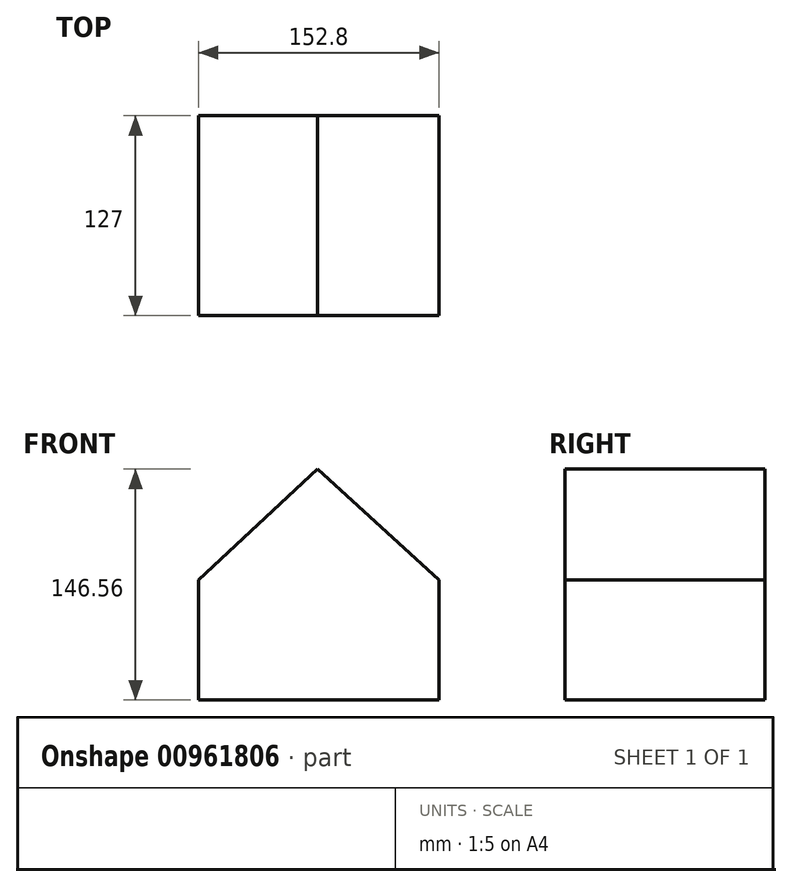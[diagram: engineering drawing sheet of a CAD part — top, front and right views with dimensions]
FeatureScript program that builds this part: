
annotation { "Feature Type Name" : "Feature", "Feature Type Description" : "" }
export const myFeature = defineFeature(function(context is Context, id is Id, definition is map)
    precondition{}
    {
        {
            var Q0;
            Q0=qCreatedBy(makeId("Front.planeOp"),FACE);
            var sketch = newSketch(context, id + "F0", { "sketchPlane" : qUnion([Q0])});
            skLineSegment(sketch, "E0", {"start": v(-75.58, 0) * mm, "end": v(0, 70.33) * mm});
            skLineSegment(sketch, "E1", {"start": v(0, 70.33) * mm, "end": v(77.22, 0) * mm});
            skLineSegment(sketch, "E2", {"start": v(-75.58, 0) * mm, "end": v(-75.58, -76.23) * mm});
            skLineSegment(sketch, "E3", {"start": v(-75.58, -76.23) * mm, "end": v(77.22, -76.23) * mm});
            skLineSegment(sketch, "E4", {"start": v(77.22, -3.11) * mm, "end": v(77.22, -76.23) * mm});
            skLineSegment(sketch, "E5", {"start": v(77.22, -3.11) * mm, "end": v(77.22, 0) * mm});
            skSolve(sketch);
        }
        {
            var Q0;
            Q0=makeQuery(id+"F0.imprint","IMPRINT",FACE,{"disambiguationData":[TD([[makeQuery(id+"F0.imprint","IMPRINT",EDGE,{"derivedFrom":sQuery(id+"F0.wireOp",EDGE,"E0")}),-1.0]])]});
            extrude(context, id + "F1", {"entities" : qUnion([Q0]), "depth" : 127 * mm, "offsetDistance" : 25.4 * mm});
        }
    });
